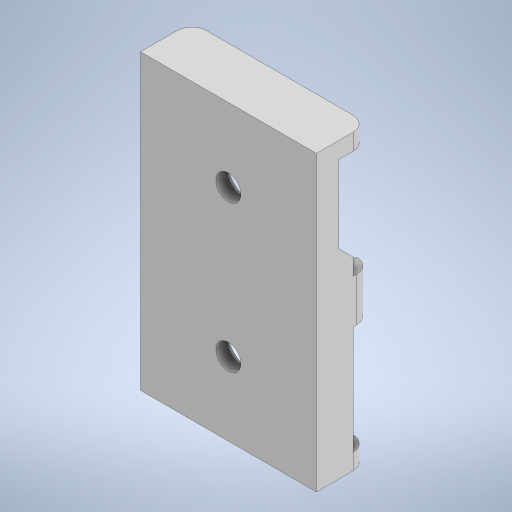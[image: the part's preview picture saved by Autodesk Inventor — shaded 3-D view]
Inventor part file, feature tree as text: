
AUTODESK INVENTOR PART (.ipt)
format: ipt  version: 2024 (Build 280153000, 153)  size: 337,920 bytes
history: native  units: mm
features: sketch x9, extrude x8, chamfer x1, fillet x1, hole x1
ambient origin geometry x8: Origin, YZ Plane, XZ Plane, XY Plane, X Axis, Y Axis, Z Axis, Center Point
bodies: Volumenkörper1 (feature_tree)
feature tree (20):
  extrude  "Extrusion1"  Depth=24.0mm
  extrude  "Extrusion2"  Depth=2.25mm
  extrude  "Extrusion4"  Depth=4.0mm TaperAngle=0.0deg
  extrude  "Extrusion5"  Depth=4.0mm
  extrude  "Extrusion6"  Depth=20.0mm
  extrude  "Extrusion7"  Depth=2.0mm TaperAngle=0.0deg
  extrude  "Extrusion8"  Depth=1.8mm
  extrude  "Extrusion9"  Depth=6.0mm
  chamfer  "Fasen1"  Distance=2.5mm
  fillet  "Rundung1"  Radius=0.8mm
  hole  "Bohrung1"  [1 undecoded]
  sketch  "Skizze1"  dims[d0=40.0mm d1=24.0mm]
  sketch  "Skizze2"  dims[d2=3.0mm d3=0.0mm d4=2.25mm]
  sketch  "Skizze4"  dims[d5=2.25mm d6=4.0mm d7=0.0mm]
  sketch  "Skizze5"  dims[d25=25.0mm d26=4.0mm]
  sketch  "Skizze6"  dims[d27=4.0mm d29=20.0mm]
  sketch  "Skizze7"  dims[d30=10.0mm d31=2.0mm d32=0.0mm]
  sketch  "Skizze9"  dims[d33=3.0mm d34=1.8mm]
  sketch  "Skizze11"  dims[d35=1.8mm d36=6.0mm d37=2.5mm d38=0.0mm d39=0.8mm]
  sketch  "Skizze12"  dims[d40=1.0mm d41=0.0mm d42=1.0mm d43=1.0mm d44=10.0mm d45=0.0mm d46=1.7mm d47=0.5mm d48=0.0mm d49=0.5mm d50=10.0mm d51=0.0mm d52=2.0mm d53=2.0mm d54=45.0deg d55=2.0mm d56=4.0mm d57=4.0mm d58=20.0mm d59=3.4mm d60=6.0mm d61=6.3mm d62=2.0mm d63=90.0deg d64=8.8mm d65=20.594885mm]
note: 1 required parameter value undecoded (feature->parameter linkage not recoverable at this tier; creation-order binding heuristic only, values carry confidence <= 0.55)
